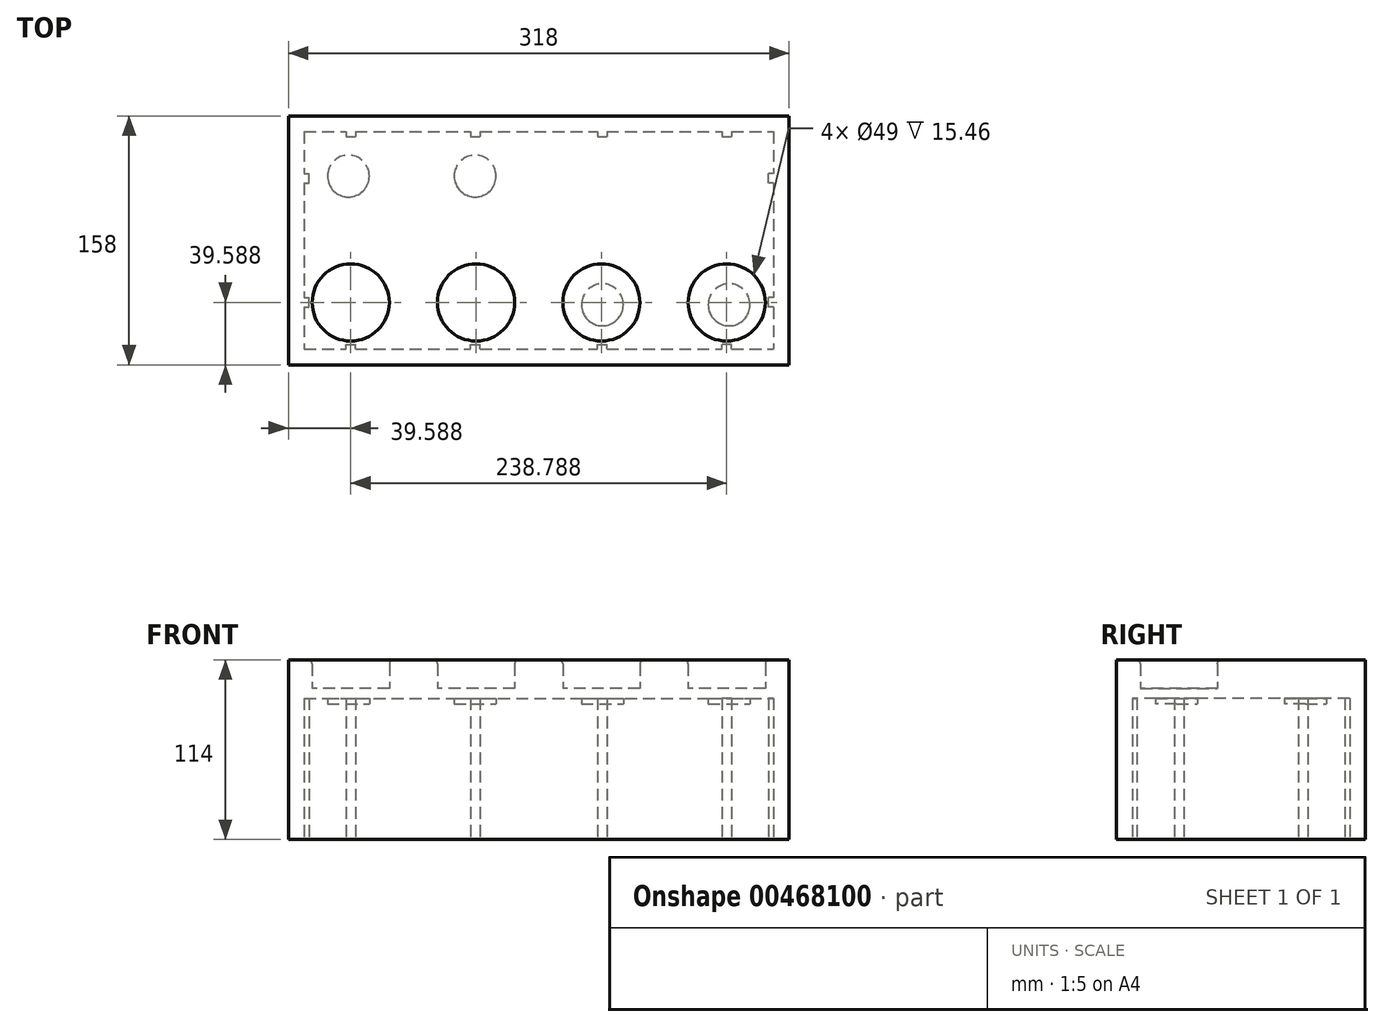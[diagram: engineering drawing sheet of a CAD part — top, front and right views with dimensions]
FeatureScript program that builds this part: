
annotation { "Feature Type Name" : "Feature", "Feature Type Description" : "" }
export const myFeature = defineFeature(function(context is Context, id is Id, definition is map)
    precondition{}
    {
        {
            var Q0;
            Q0=qCreatedBy(makeId("Top.planeOp"),FACE);
            var sketch = newSketch(context, id + "F0", { "sketchPlane" : qUnion([Q0])});
            skLineSegment(sketch, "E0.bottom", {"start": v(-159, 79) * mm, "end": v(159, 79) * mm});
            skLineSegment(sketch, "E0.top", {"start": v(-159, -79) * mm, "end": v(159, -79) * mm});
            skLineSegment(sketch, "E0.left", {"start": v(-159, 79) * mm, "end": v(-159, -79) * mm});
            skLineSegment(sketch, "E0.right", {"start": v(159, 79) * mm, "end": v(159, -79) * mm});
            skSolve(sketch);
        }
        {
            var Q0;
            Q0=makeQuery(id+"F0.imprint","IMPRINT",FACE,{"disambiguationData":[TD([[makeQuery(id+"F0.imprint","IMPRINT",EDGE,{"derivedFrom":sQuery(id+"F0.wireOp",EDGE,"E0.bottom")}),-1.0]])]});
            extrude(context, id + "F1", {"entities" : qUnion([Q0]), "depth" : 96 * mm});
        }
        {
            var Q0;
            Q0=makeQuery(id+"F1.opExtrude","CAP_FACE",FACE,{"disambiguationData":[OSD([sQuery(id+"F0.wireOp",EDGE,"E0.bottom"),sQuery(id+"F0.wireOp",EDGE,"E0.top"),sQuery(id+"F0.wireOp",EDGE,"E0.left"),sQuery(id+"F0.wireOp",EDGE,"E0.right")])],"isStart":true});
            shell(context, id + "F2", {"entities" : qUnion([Q0]), "thickness" : 10 * mm});
        }
        {
            var Q0;
            Q0=qCreatedBy(makeId("Top.planeOp"),FACE);
            var sketch = newSketch(context, id + "F3", { "sketchPlane" : qUnion([Q0])});
            skCircle(sketch, "E1", {"center": v(-80, 0) * mm, "radius": 32.05 * mm});
            skCircle(sketch, "E2", {"center": v(0, 0) * mm, "radius": 32.05 * mm});
            skCircle(sketch, "E3", {"center": v(80, 0) * mm, "radius": 32.05 * mm});
            skCircle(sketch, "E4", {"center": v(-80, 0) * mm, "radius": 24.5 * mm});
            skCircle(sketch, "E5", {"center": v(0, 0) * mm, "radius": 24.5 * mm});
            skCircle(sketch, "E6", {"center": v(80, 0) * mm, "radius": 24.5 * mm});
            skSolve(sketch);
        }
        {
            var Q0;
            Q0=makeQuery(id+"F3.imprint","IMPRINT",FACE,{"disambiguationData":[TD([[makeQuery(id+"F3.imprint","IMPRINT",EDGE,{"derivedFrom":sQuery(id+"F3.wireOp",EDGE,"E1")}),1.0]])]});
            var Q1;
            Q1=makeQuery(id+"F3.imprint","IMPRINT",FACE,{"disambiguationData":[TD([[makeQuery(id+"F3.imprint","IMPRINT",EDGE,{"derivedFrom":sQuery(id+"F3.wireOp",EDGE,"E2")}),1.0]])]});
            var Q2;
            Q2=makeQuery(id+"F3.imprint","IMPRINT",FACE,{"disambiguationData":[TD([[makeQuery(id+"F3.imprint","IMPRINT",EDGE,{"derivedFrom":sQuery(id+"F3.wireOp",EDGE,"E3")}),1.0]])]});
            extrude(context, id + "F4", {"entities" : qUnion([Q0, Q1, Q2]), "operationType" : NewBodyOperationType.ADD, "depth" : 94.74 * mm});
        }
        {
            var Q0;
            Q0=makeQuery(id+"F1.opExtrude","CAP_FACE",FACE,{"disambiguationData":[OSD([sQuery(id+"F0.wireOp",EDGE,"E0.bottom"),sQuery(id+"F0.wireOp",EDGE,"E0.top"),sQuery(id+"F0.wireOp",EDGE,"E0.left"),sQuery(id+"F0.wireOp",EDGE,"E0.right")])],"isStart":false});
            var sketch = newSketch(context, id + "F5", { "sketchPlane" : qUnion([Q0])});
            skCircle(sketch, "E7", {"center": v(-119.41, 39.41) * mm, "radius": 24.5 * mm});
            skCircle(sketch, "E8.1.0.0", {"center": v(-39.82, 39.41) * mm, "radius": 24.5 * mm});
            skCircle(sketch, "E8.2.0.0", {"center": v(39.78, 39.41) * mm, "radius": 24.5 * mm});
            skCircle(sketch, "E8.3.0.0", {"center": v(119.38, 39.41) * mm, "radius": 24.5 * mm});
            skLineSegment(sketch, "E8.direction1", {"start": v(-119.41, 39.41) * mm, "end": v(-39.82, 39.41) * mm, "construction": true});
            skLineSegment(sketch, "E9", {"start": v(-202.86, 0) * mm, "end": v(192.54, 0) * mm, "construction": true});
            skCircle(sketch, "E10.MirrorC", {"center": v(-119.41, -39.41) * mm, "radius": 24.5 * mm});
            skCircle(sketch, "E11.MirrorC", {"center": v(-39.82, -39.41) * mm, "radius": 24.5 * mm});
            skCircle(sketch, "E12.MirrorC", {"center": v(39.78, -39.41) * mm, "radius": 24.5 * mm});
            skCircle(sketch, "E13.MirrorC", {"center": v(119.38, -39.41) * mm, "radius": 24.5 * mm});
            skLineSegment(sketch, "E14", {"start": v(-186, 39.41) * mm, "end": v(210.43, 39.41) * mm, "construction": true});
            skLineSegment(sketch, "E15", {"start": v(-186.7, -39.41) * mm, "end": v(216.66, -39.41) * mm, "construction": true});
            skLineSegment(sketch, "E16", {"start": v(-119.41, 108.26) * mm, "end": v(-119.41, -106.32) * mm, "construction": true});
            skLineSegment(sketch, "E17", {"start": v(119.38, 102.92) * mm, "end": v(119.38, -102.76) * mm, "construction": true});
            skLineSegment(sketch, "E18", {"start": v(-39.82, 109.65) * mm, "end": v(-39.82, -100.32) * mm, "construction": true});
            skLineSegment(sketch, "E19", {"start": v(39.78, 106.53) * mm, "end": v(39.78, -109.25) * mm, "construction": true});
            skSolve(sketch);
        }
        {
            var Q0;
            Q0=makeQuery(id+"F5.imprint","IMPRINT",FACE,{"disambiguationData":[TD([[makeQuery(id+"F5.imprint","IMPRINT",EDGE,{"derivedFrom":sQuery(id+"F5.wireOp",EDGE,"E7")}),1.0]])]});
            var Q1;
            Q1=makeQuery(id+"F5.imprint","IMPRINT",FACE,{"disambiguationData":[TD([[makeQuery(id+"F5.imprint","IMPRINT",EDGE,{"derivedFrom":sQuery(id+"F5.wireOp",EDGE,"E8.1.0.0")}),1.0]])]});
            var Q2;
            Q2=makeQuery(id+"F5.imprint","IMPRINT",FACE,{"disambiguationData":[TD([[makeQuery(id+"F5.imprint","IMPRINT",EDGE,{"derivedFrom":sQuery(id+"F5.wireOp",EDGE,"E8.2.0.0")}),1.0]])]});
            var Q3;
            Q3=makeQuery(id+"F5.imprint","IMPRINT",FACE,{"disambiguationData":[TD([[makeQuery(id+"F5.imprint","IMPRINT",EDGE,{"derivedFrom":sQuery(id+"F5.wireOp",EDGE,"E8.3.0.0")}),1.0]])]});
            var Q4;
            Q4=makeQuery(id+"F5.imprint","IMPRINT",FACE,{"disambiguationData":[TD([[makeQuery(id+"F5.imprint","IMPRINT",EDGE,{"derivedFrom":sQuery(id+"F5.wireOp",EDGE,"E13.MirrorC")}),-1.0]])]});
            var Q5;
            Q5=makeQuery(id+"F5.imprint","IMPRINT",FACE,{"disambiguationData":[TD([[makeQuery(id+"F5.imprint","IMPRINT",EDGE,{"derivedFrom":sQuery(id+"F5.wireOp",EDGE,"E12.MirrorC")}),-1.0]])]});
            var Q6;
            Q6=makeQuery(id+"F5.imprint","IMPRINT",FACE,{"disambiguationData":[TD([[makeQuery(id+"F5.imprint","IMPRINT",EDGE,{"derivedFrom":sQuery(id+"F5.wireOp",EDGE,"E11.MirrorC")}),-1.0]])]});
            var Q7;
            Q7=makeQuery(id+"F5.imprint","IMPRINT",FACE,{"disambiguationData":[TD([[makeQuery(id+"F5.imprint","IMPRINT",EDGE,{"derivedFrom":sQuery(id+"F5.wireOp",EDGE,"E10.MirrorC")}),-1.0]])]});
            extrude(context, id + "F6", {"entities" : qUnion([Q0, Q1, Q2, Q3, Q4, Q5, Q6, Q7]), "operationType" : NewBodyOperationType.ADD, "depth" : 18 * mm});
        }
        {
            var Q0;
            Q0=makeQuery(id+"F4.boolean.opBoolean","MERGE",FACE,{"derivedFrom":[makeQuery(id+"F1.opExtrude","CAP_FACE",FACE,{"disambiguationData":[OSD([sQuery(id+"F0.wireOp",EDGE,"E0.bottom"),sQuery(id+"F0.wireOp",EDGE,"E0.top"),sQuery(id+"F0.wireOp",EDGE,"E0.left"),sQuery(id+"F0.wireOp",EDGE,"E0.right")])],"isStart":true}),makeQuery(id+"F4.opExtrude","CAP_FACE",FACE,{"disambiguationData":[OSD([sQuery(id+"F9.wireOp",EDGE,"E38.bottom"),sQuery(id+"F9.wireOp",EDGE,"E38.top"),sQuery(id+"F9.wireOp",EDGE,"E38.left"),sQuery(id+"F9.wireOp",EDGE,"E38.right")])],"isStart":true}),makeQuery(id+"F4.opExtrude","CAP_FACE",FACE,{"disambiguationData":[OSD([sQuery(id+"F3.wireOp",EDGE,"E2"),sQuery(id+"F3.wireOp",EDGE,"E5")])],"isStart":true})]});
            var sketch = newSketch(context, id + "F7", { "sketchPlane" : qUnion([Q0])});
            skLineSegment(sketch, "E20.bottom", {"start": v(-122.42, 73.6) * mm, "end": v(-116.42, 73.6) * mm});
            skLineSegment(sketch, "E20.top", {"start": v(-122.42, 66) * mm, "end": v(-116.42, 66) * mm});
            skLineSegment(sketch, "E20.left", {"start": v(-122.42, 73.6) * mm, "end": v(-122.42, 66) * mm});
            skLineSegment(sketch, "E20.right", {"start": v(-116.42, 73.6) * mm, "end": v(-116.42, 66) * mm});
            skLineSegment(sketch, "E21.bottom", {"start": v(-154.66, 42.42) * mm, "end": v(-146, 42.42) * mm});
            skLineSegment(sketch, "E21.top", {"start": v(-154.66, 36.42) * mm, "end": v(-146, 36.42) * mm});
            skLineSegment(sketch, "E21.left", {"start": v(-154.66, 42.42) * mm, "end": v(-154.66, 36.42) * mm});
            skLineSegment(sketch, "E21.right", {"start": v(-146, 42.42) * mm, "end": v(-146, 36.42) * mm});
            skLineSegment(sketch, "E22.bottom", {"start": v(-154.5, -36.42) * mm, "end": v(-146, -36.42) * mm});
            skLineSegment(sketch, "E22.top", {"start": v(-154.5, -42.42) * mm, "end": v(-146, -42.42) * mm});
            skLineSegment(sketch, "E22.left", {"start": v(-154.5, -36.42) * mm, "end": v(-154.5, -42.42) * mm});
            skLineSegment(sketch, "E22.right", {"start": v(-146, -36.42) * mm, "end": v(-146, -42.42) * mm});
            skLineSegment(sketch, "E23.bottom", {"start": v(-122.42, -72.53) * mm, "end": v(-116.42, -72.53) * mm});
            skLineSegment(sketch, "E23.top", {"start": v(-122.42, -66) * mm, "end": v(-116.42, -66) * mm});
            skLineSegment(sketch, "E23.left", {"start": v(-122.42, -72.53) * mm, "end": v(-122.42, -66) * mm});
            skLineSegment(sketch, "E23.right", {"start": v(-116.42, -72.53) * mm, "end": v(-116.42, -66) * mm});
            skLineSegment(sketch, "E24.bottom", {"start": v(122.42, 74.33) * mm, "end": v(116.42, 74.33) * mm});
            skLineSegment(sketch, "E24.top", {"start": v(122.42, 66) * mm, "end": v(116.42, 66) * mm});
            skLineSegment(sketch, "E24.left", {"start": v(122.42, 74.33) * mm, "end": v(122.42, 66) * mm});
            skLineSegment(sketch, "E24.right", {"start": v(116.42, 74.33) * mm, "end": v(116.42, 66) * mm});
            skLineSegment(sketch, "E25.bottom", {"start": v(152.85, 42.42) * mm, "end": v(146, 42.42) * mm});
            skLineSegment(sketch, "E25.top", {"start": v(152.85, 36.42) * mm, "end": v(146, 36.42) * mm});
            skLineSegment(sketch, "E25.left", {"start": v(152.85, 42.42) * mm, "end": v(152.85, 36.42) * mm});
            skLineSegment(sketch, "E25.right", {"start": v(146, 42.42) * mm, "end": v(146, 36.42) * mm});
            skLineSegment(sketch, "E26.bottom", {"start": v(116.42, -72.71) * mm, "end": v(122.42, -72.71) * mm});
            skLineSegment(sketch, "E26.top", {"start": v(116.42, -66) * mm, "end": v(122.42, -66) * mm});
            skLineSegment(sketch, "E26.left", {"start": v(116.42, -72.71) * mm, "end": v(116.42, -66) * mm});
            skLineSegment(sketch, "E26.right", {"start": v(122.42, -72.71) * mm, "end": v(122.42, -66) * mm});
            skLineSegment(sketch, "E27.bottom", {"start": v(153.22, -36.42) * mm, "end": v(146, -36.42) * mm});
            skLineSegment(sketch, "E27.top", {"start": v(153.22, -42.42) * mm, "end": v(146, -42.42) * mm});
            skLineSegment(sketch, "E27.left", {"start": v(153.22, -36.42) * mm, "end": v(153.22, -42.42) * mm});
            skLineSegment(sketch, "E27.right", {"start": v(146, -36.42) * mm, "end": v(146, -42.42) * mm});
            skLineSegment(sketch, "E28.bottom", {"start": v(-43.28, 73.4) * mm, "end": v(-37.28, 73.4) * mm});
            skLineSegment(sketch, "E28.top", {"start": v(-43.28, 66) * mm, "end": v(-37.28, 66) * mm});
            skLineSegment(sketch, "E28.left", {"start": v(-43.28, 73.4) * mm, "end": v(-43.28, 66) * mm});
            skLineSegment(sketch, "E28.right", {"start": v(-37.28, 73.4) * mm, "end": v(-37.28, 66) * mm});
            skLineSegment(sketch, "E29.MirrorCS", {"start": v(-43.28, -66) * mm, "end": v(-37.28, -66) * mm});
            skLineSegment(sketch, "E30.MirrorCS", {"start": v(-43.28, -73.4) * mm, "end": v(-43.28, -66) * mm});
            skLineSegment(sketch, "E31.MirrorCS", {"start": v(-37.28, -73.4) * mm, "end": v(-37.28, -66) * mm});
            skLineSegment(sketch, "E32.MirrorCS", {"start": v(-43.28, -73.4) * mm, "end": v(-37.28, -73.4) * mm});
            skLineSegment(sketch, "E33.bottom", {"start": v(37.28, 73.15) * mm, "end": v(43.28, 73.15) * mm});
            skLineSegment(sketch, "E33.top", {"start": v(37.28, 66) * mm, "end": v(43.28, 66) * mm});
            skLineSegment(sketch, "E33.left", {"start": v(37.28, 73.15) * mm, "end": v(37.28, 66) * mm});
            skLineSegment(sketch, "E33.right", {"start": v(43.28, 73.15) * mm, "end": v(43.28, 66) * mm});
            skLineSegment(sketch, "E34.MirrorCS", {"start": v(43.28, -73.15) * mm, "end": v(43.28, -66) * mm});
            skLineSegment(sketch, "E35.MirrorCS", {"start": v(37.28, -73.15) * mm, "end": v(37.28, -66) * mm});
            skLineSegment(sketch, "E36.MirrorCS", {"start": v(37.28, -66) * mm, "end": v(43.28, -66) * mm});
            skLineSegment(sketch, "E37.MirrorCS", {"start": v(37.28, -73.15) * mm, "end": v(43.28, -73.15) * mm});
            skSolve(sketch);
        }
        {
            var Q0;
            {var subQ0=sQuery(id+"F7.wireOp",EDGE,"E33.top");Q0=makeQuery(id+"F7.imprint","IMPRINT",FACE,{"disambiguationData":[TD([[makeQuery(id+"F7.imprint","IMPRINT",EDGE,{"derivedFrom":subQ0}),1.0]])]});}
            var Q1;
            {var subQ0=sQuery(id+"F7.wireOp",EDGE,"E24.top");Q1=makeQuery(id+"F7.imprint","IMPRINT",FACE,{"disambiguationData":[TD([[makeQuery(id+"F7.imprint","IMPRINT",EDGE,{"derivedFrom":subQ0}),-1.0]])]});}
            var Q2;
            {var subQ0=sQuery(id+"F7.wireOp",EDGE,"E25.right");Q2=makeQuery(id+"F7.imprint","IMPRINT",FACE,{"disambiguationData":[TD([[makeQuery(id+"F7.imprint","IMPRINT",EDGE,{"derivedFrom":subQ0}),1.0]])]});}
            var Q3;
            {var subQ0=sQuery(id+"F7.wireOp",EDGE,"E28.top");Q3=makeQuery(id+"F7.imprint","IMPRINT",FACE,{"disambiguationData":[TD([[makeQuery(id+"F7.imprint","IMPRINT",EDGE,{"derivedFrom":subQ0}),1.0]])]});}
            var Q4;
            {var subQ0=sQuery(id+"F7.wireOp",EDGE,"E20.top");Q4=makeQuery(id+"F7.imprint","IMPRINT",FACE,{"disambiguationData":[TD([[makeQuery(id+"F7.imprint","IMPRINT",EDGE,{"derivedFrom":subQ0}),1.0]])]});}
            var Q5;
            {var subQ0=sQuery(id+"F7.wireOp",EDGE,"E21.right");Q5=makeQuery(id+"F7.imprint","IMPRINT",FACE,{"disambiguationData":[TD([[makeQuery(id+"F7.imprint","IMPRINT",EDGE,{"derivedFrom":subQ0}),-1.0]])]});}
            var Q6;
            {var subQ0=sQuery(id+"F7.wireOp",EDGE,"E22.right");Q6=makeQuery(id+"F7.imprint","IMPRINT",FACE,{"disambiguationData":[TD([[makeQuery(id+"F7.imprint","IMPRINT",EDGE,{"derivedFrom":subQ0}),-1.0]])]});}
            var Q7;
            {var subQ0=sQuery(id+"F7.wireOp",EDGE,"E23.top");Q7=makeQuery(id+"F7.imprint","IMPRINT",FACE,{"disambiguationData":[TD([[makeQuery(id+"F7.imprint","IMPRINT",EDGE,{"derivedFrom":subQ0}),-1.0]])]});}
            var Q8;
            {var subQ0=sQuery(id+"F7.wireOp",EDGE,"E29.MirrorCS");Q8=makeQuery(id+"F7.imprint","IMPRINT",FACE,{"disambiguationData":[TD([[makeQuery(id+"F7.imprint","IMPRINT",EDGE,{"derivedFrom":subQ0}),-1.0]])]});}
            var Q9;
            {var subQ0=sQuery(id+"F7.wireOp",EDGE,"E36.MirrorCS");Q9=makeQuery(id+"F7.imprint","IMPRINT",FACE,{"disambiguationData":[TD([[makeQuery(id+"F7.imprint","IMPRINT",EDGE,{"derivedFrom":subQ0}),-1.0]])]});}
            var Q10;
            {var subQ0=sQuery(id+"F7.wireOp",EDGE,"E26.top");Q10=makeQuery(id+"F7.imprint","IMPRINT",FACE,{"disambiguationData":[TD([[makeQuery(id+"F7.imprint","IMPRINT",EDGE,{"derivedFrom":subQ0}),-1.0]])]});}
            var Q11;
            {var subQ0=sQuery(id+"F7.wireOp",EDGE,"E27.right");Q11=makeQuery(id+"F7.imprint","IMPRINT",FACE,{"disambiguationData":[TD([[makeQuery(id+"F7.imprint","IMPRINT",EDGE,{"derivedFrom":subQ0}),1.0]])]});}
            extrude(context, id + "F8", {"entities" : qUnion([Q0, Q1, Q2, Q3, Q4, Q5, Q6, Q7, Q8, Q9, Q10, Q11]), "operationType" : NewBodyOperationType.ADD, "oppositeDirection" : true, "depth" : 96 * mm});
        }
        {
            var Q0;
            Q0=qCreatedBy(makeId("Top.planeOp"),FACE);
            var sketch = newSketch(context, id + "F9", { "sketchPlane" : qUnion([Q0])});
            skLineSegment(sketch, "E38.bottom", {"start": v(-4.45, -79) * mm, "end": v(3.55, -79) * mm});
            skLineSegment(sketch, "E38.top", {"start": v(-4.45, 79) * mm, "end": v(3.55, 79) * mm});
            skLineSegment(sketch, "E38.left", {"start": v(-4.45, -79) * mm, "end": v(-4.45, -31.74) * mm});
            skLineSegment(sketch, "E38.right", {"start": v(3.55, -79) * mm, "end": v(3.55, -31.85) * mm});
            skArc(sketch, "E39.0", {"start": v(-4.45, -31.74) * mm, "mid": v(-0.45, -32.05) * mm, "end": v(3.55, -31.85) * mm});
            skLineSegment(sketch, "E40.trimOffspring", {"start": v(3.55, 31.85) * mm, "end": v(3.55, 79) * mm});
            skLineSegment(sketch, "E41.trimOffspring", {"start": v(-4.45, 31.74) * mm, "end": v(-4.45, 79) * mm});
            skArc(sketch, "E42.trimOffspring", {"start": v(3.55, 31.85) * mm, "mid": v(-0.45, 32.05) * mm, "end": v(-4.45, 31.74) * mm});
            skSolve(sketch);
        }
        {
            var Q0;
            Q0=qSketchRegion(id+"F9",true);
            var Q1;
            {var subQ0=sQuery(id+"F0.wireOp",EDGE,"E0.right");var subQ1=sQuery(id+"F0.wireOp",EDGE,"E0.left");var subQ2=sQuery(id+"F0.wireOp",EDGE,"E0.top");var subQ3=sQuery(id+"F0.wireOp",EDGE,"E0.bottom");Q1=makeQuery(id+"F4.boolean.opBoolean","SPLIT",FACE,{"disambiguationData":[TD([makeQuery(id+"F2.opShell","OFFSET_FACE",FACE,{"disambiguationData":[OSD([subQ3])]})])],"derivedFrom":makeQuery(id+"F2.opShell","OFFSET_FACE",FACE,{"disambiguationData":[OSD([subQ3,subQ2,subQ1,subQ0])]})});}
            extrude(context, id + "F10", {"entities" : qUnion([Q0]), "operationType" : NewBodyOperationType.ADD, "endBound" : BoundingType.UP_TO_SURFACE, "endBoundEntityFace" : qUnion([Q1]), "depth" : 25.4 * mm, "hasSecondDirection" : true, "secondDirectionOppositeDirection" : false, "secondDirectionDepth" : 6.6 * mm});
        }
        {
            var Q0;
            Q0=makeQuery(id+"F6.opExtrude","CAP_EDGE",EDGE,{"disambiguationData":[OSD([sQuery(id+"F5.wireOp",EDGE,"E10.MirrorC")])],"isStart":false});
            var Q1;
            Q1=makeQuery(id+"F6.opExtrude","CAP_EDGE",EDGE,{"disambiguationData":[OSD([sQuery(id+"F5.wireOp",EDGE,"E7")])],"isStart":false});
            var Q2;
            Q2=makeQuery(id+"F6.opExtrude","CAP_EDGE",EDGE,{"disambiguationData":[OSD([sQuery(id+"F5.wireOp",EDGE,"E8.1.0.0")])],"isStart":false});
            var Q3;
            Q3=makeQuery(id+"F6.opExtrude","CAP_EDGE",EDGE,{"disambiguationData":[OSD([sQuery(id+"F5.wireOp",EDGE,"E11.MirrorC")])],"isStart":false});
            var Q4;
            Q4=makeQuery(id+"F6.opExtrude","CAP_EDGE",EDGE,{"disambiguationData":[OSD([sQuery(id+"F5.wireOp",EDGE,"E12.MirrorC")])],"isStart":false});
            var Q5;
            Q5=makeQuery(id+"F6.opExtrude","CAP_EDGE",EDGE,{"disambiguationData":[OSD([sQuery(id+"F5.wireOp",EDGE,"E8.2.0.0")])],"isStart":false});
            var Q6;
            Q6=makeQuery(id+"F6.opExtrude","CAP_EDGE",EDGE,{"disambiguationData":[OSD([sQuery(id+"F5.wireOp",EDGE,"E8.3.0.0")])],"isStart":false});
            var Q7;
            Q7=makeQuery(id+"F6.opExtrude","CAP_EDGE",EDGE,{"disambiguationData":[OSD([sQuery(id+"F5.wireOp",EDGE,"E13.MirrorC")])],"isStart":false});
            var Q8;
            Q8=makeQuery(id+"F6.opExtrude","CAP_EDGE",EDGE,{"disambiguationData":[OSD([sQuery(id+"F5.wireOp",EDGE,"E13.MirrorC")])],"isStart":true});
            var Q9;
            Q9=makeQuery(id+"F6.opExtrude","CAP_EDGE",EDGE,{"disambiguationData":[OSD([sQuery(id+"F5.wireOp",EDGE,"E8.3.0.0")])],"isStart":true});
            var Q10;
            Q10=makeQuery(id+"F6.opExtrude","CAP_EDGE",EDGE,{"disambiguationData":[OSD([sQuery(id+"F5.wireOp",EDGE,"E12.MirrorC")])],"isStart":true});
            var Q11;
            Q11=makeQuery(id+"F6.opExtrude","CAP_EDGE",EDGE,{"disambiguationData":[OSD([sQuery(id+"F5.wireOp",EDGE,"E11.MirrorC")])],"isStart":true});
            var Q12;
            Q12=makeQuery(id+"F6.opExtrude","CAP_EDGE",EDGE,{"disambiguationData":[OSD([sQuery(id+"F5.wireOp",EDGE,"E10.MirrorC")])],"isStart":true});
            var Q13;
            Q13=makeQuery(id+"F6.opExtrude","CAP_EDGE",EDGE,{"disambiguationData":[OSD([sQuery(id+"F5.wireOp",EDGE,"E7")])],"isStart":true});
            var Q14;
            Q14=makeQuery(id+"F6.opExtrude","CAP_EDGE",EDGE,{"disambiguationData":[OSD([sQuery(id+"F5.wireOp",EDGE,"E8.1.0.0")])],"isStart":true});
            var Q15;
            Q15=makeQuery(id+"F6.opExtrude","CAP_EDGE",EDGE,{"disambiguationData":[OSD([sQuery(id+"F5.wireOp",EDGE,"E8.2.0.0")])],"isStart":true});
            fillet(context, id + "F11", {"entities" : qUnion([Q0, Q1, Q2, Q3, Q4, Q5, Q6, Q7, Q8, Q9, Q10, Q11, Q12, Q13, Q14, Q15]), "radius" : 2.54 * mm, "tangentPropagation" : true, "allowEdgeOverflow" : false});
        }
        {
            var Q0;
            {var subQ0=sQuery(id+"F0.wireOp",EDGE,"E0.bottom");var subQ1=sQuery(id+"F0.wireOp",EDGE,"E0.top");var subQ2=sQuery(id+"F0.wireOp",EDGE,"E0.right");var subQ3=sQuery(id+"F0.wireOp",EDGE,"E0.left");Q0=makeQuery(id+"F8.boolean.opBoolean","MERGE",FACE,{"derivedFrom":[makeQuery(id+"F1.opExtrude","CAP_FACE",FACE,{"disambiguationData":[OSD([subQ0,subQ1,subQ3,subQ2])],"isStart":true}),makeQuery(id+"F8.opExtrude","CAP_FACE",FACE,{"disambiguationData":[OSD([subQ1,sQuery(id+"F7.wireOp",EDGE,"E20.top"),sQuery(id+"F7.wireOp",EDGE,"E20.left"),sQuery(id+"F7.wireOp",EDGE,"E20.right")])],"isStart":true}),makeQuery(id+"F8.opExtrude","CAP_FACE",FACE,{"disambiguationData":[OSD([subQ3,sQuery(id+"F7.wireOp",EDGE,"E21.bottom"),sQuery(id+"F7.wireOp",EDGE,"E21.top"),sQuery(id+"F7.wireOp",EDGE,"E21.right")])],"isStart":true}),makeQuery(id+"F8.opExtrude","CAP_FACE",FACE,{"disambiguationData":[OSD([subQ3,sQuery(id+"F7.wireOp",EDGE,"E22.bottom"),sQuery(id+"F7.wireOp",EDGE,"E22.top"),sQuery(id+"F7.wireOp",EDGE,"E22.right")])],"isStart":true}),makeQuery(id+"F8.opExtrude","CAP_FACE",FACE,{"disambiguationData":[OSD([subQ0,sQuery(id+"F7.wireOp",EDGE,"E23.top"),sQuery(id+"F7.wireOp",EDGE,"E23.left"),sQuery(id+"F7.wireOp",EDGE,"E23.right")])],"isStart":true}),makeQuery(id+"F8.opExtrude","CAP_FACE",FACE,{"disambiguationData":[OSD([subQ1,sQuery(id+"F7.wireOp",EDGE,"E24.top"),sQuery(id+"F7.wireOp",EDGE,"E24.left"),sQuery(id+"F7.wireOp",EDGE,"E24.right")])],"isStart":true}),makeQuery(id+"F8.opExtrude","CAP_FACE",FACE,{"disambiguationData":[OSD([subQ2,sQuery(id+"F7.wireOp",EDGE,"E25.bottom"),sQuery(id+"F7.wireOp",EDGE,"E25.top"),sQuery(id+"F7.wireOp",EDGE,"E25.right")])],"isStart":true}),makeQuery(id+"F8.opExtrude","CAP_FACE",FACE,{"disambiguationData":[OSD([subQ0,sQuery(id+"F7.wireOp",EDGE,"E26.top"),sQuery(id+"F7.wireOp",EDGE,"E26.left"),sQuery(id+"F7.wireOp",EDGE,"E26.right")])],"isStart":true}),makeQuery(id+"F8.opExtrude","CAP_FACE",FACE,{"disambiguationData":[OSD([subQ2,sQuery(id+"F7.wireOp",EDGE,"E27.bottom"),sQuery(id+"F7.wireOp",EDGE,"E27.top"),sQuery(id+"F7.wireOp",EDGE,"E27.right")])],"isStart":true}),makeQuery(id+"F8.opExtrude","CAP_FACE",FACE,{"disambiguationData":[OSD([subQ1,sQuery(id+"F7.wireOp",EDGE,"E28.top"),sQuery(id+"F7.wireOp",EDGE,"E28.left"),sQuery(id+"F7.wireOp",EDGE,"E28.right")])],"isStart":true}),makeQuery(id+"F8.opExtrude","CAP_FACE",FACE,{"disambiguationData":[OSD([subQ0,sQuery(id+"F7.wireOp",EDGE,"E29.MirrorCS"),sQuery(id+"F7.wireOp",EDGE,"E30.MirrorCS"),sQuery(id+"F7.wireOp",EDGE,"E31.MirrorCS")])],"isStart":true}),makeQuery(id+"F8.opExtrude","CAP_FACE",FACE,{"disambiguationData":[OSD([subQ1,sQuery(id+"F7.wireOp",EDGE,"E33.top"),sQuery(id+"F7.wireOp",EDGE,"E33.left"),sQuery(id+"F7.wireOp",EDGE,"E33.right")])],"isStart":true}),makeQuery(id+"F8.opExtrude","CAP_FACE",FACE,{"disambiguationData":[OSD([subQ0,sQuery(id+"F7.wireOp",EDGE,"E34.MirrorCS"),sQuery(id+"F7.wireOp",EDGE,"E35.MirrorCS"),sQuery(id+"F7.wireOp",EDGE,"E36.MirrorCS")])],"isStart":true})]});}
            var sketch = newSketch(context, id + "F12", { "sketchPlane" : qUnion([Q0])});
            skCircle(sketch, "E43", {"center": v(-120.9, 40.9) * mm, "radius": 13.3 * mm});
            skLineSegment(sketch, "E44", {"start": v(-120.9, 40.9) * mm, "end": v(-120.9, 79) * mm, "construction": true});
            skLineSegment(sketch, "E45", {"start": v(-120.9, 40.9) * mm, "end": v(-159, 40.9) * mm, "construction": true});
            skLineSegment(sketch, "E46", {"start": v(-159, 0) * mm, "end": v(159, 0) * mm, "construction": true});
            skCircle(sketch, "E47.MirrorC", {"center": v(-120.9, -40.9) * mm, "radius": 13.3 * mm});
            skLineSegment(sketch, "E48", {"start": v(0, 79) * mm, "end": v(0, -79) * mm, "construction": true});
            skCircle(sketch, "E49.MirrorC", {"center": v(120.9, -40.9) * mm, "radius": 13.3 * mm});
            skCircle(sketch, "E50.MirrorC", {"center": v(120.9, 40.9) * mm, "radius": 13.3 * mm});
            skLineSegment(sketch, "E51", {"start": v(-80.77, 32.16) * mm, "end": v(0, 32.16) * mm, "construction": true});
            skLineSegment(sketch, "E52", {"start": v(-40.39, 32.16) * mm, "end": v(-40.51, 79.36) * mm, "construction": true});
            skCircle(sketch, "E53", {"center": v(-40.4, 40.9) * mm, "radius": 13.3 * mm});
            skLineSegment(sketch, "E54", {"start": v(-120.9, 40.9) * mm, "end": v(120.9, 40.9) * mm, "construction": true});
            skCircle(sketch, "E55.MirrorC", {"center": v(40.4, 40.9) * mm, "radius": 13.3 * mm});
            skCircle(sketch, "E56.MirrorC", {"center": v(40.4, -40.9) * mm, "radius": 13.3 * mm});
            skCircle(sketch, "E57.MirrorC", {"center": v(-40.4, -40.9) * mm, "radius": 13.3 * mm});
            skSolve(sketch);
        }
        {
            var Q0;
            Q0=makeQuery(id+"F12.imprint","IMPRINT",FACE,{"disambiguationData":[TD([[makeQuery(id+"F12.imprint","IMPRINT",EDGE,{"derivedFrom":sQuery(id+"F12.wireOp",EDGE,"E49.MirrorC")}),1.0]])]});
            var Q1;
            Q1=makeQuery(id+"F12.imprint","IMPRINT",FACE,{"disambiguationData":[TD([[makeQuery(id+"F12.imprint","IMPRINT",EDGE,{"derivedFrom":sQuery(id+"F12.wireOp",EDGE,"E56.MirrorC")}),1.0]])]});
            var Q2;
            Q2=makeQuery(id+"F12.imprint","IMPRINT",FACE,{"disambiguationData":[TD([[makeQuery(id+"F12.imprint","IMPRINT",EDGE,{"derivedFrom":sQuery(id+"F12.wireOp",EDGE,"E57.MirrorC")}),-1.0]])]});
            var Q3;
            Q3=makeQuery(id+"F12.imprint","IMPRINT",FACE,{"disambiguationData":[TD([[makeQuery(id+"F12.imprint","IMPRINT",EDGE,{"derivedFrom":sQuery(id+"F12.wireOp",EDGE,"E47.MirrorC")}),-1.0]])]});
            var Q4;
            Q4=makeQuery(id+"F12.imprint","IMPRINT",FACE,{"disambiguationData":[TD([[makeQuery(id+"F12.imprint","IMPRINT",EDGE,{"derivedFrom":sQuery(id+"F12.wireOp",EDGE,"E43")}),1.0]])]});
            var Q5;
            Q5=makeQuery(id+"F12.imprint","IMPRINT",FACE,{"disambiguationData":[TD([[makeQuery(id+"F12.imprint","IMPRINT",EDGE,{"derivedFrom":sQuery(id+"F12.wireOp",EDGE,"E53")}),1.0]])]});
            var Q6;
            Q6=makeQuery(id+"F12.imprint","IMPRINT",FACE,{"disambiguationData":[TD([[makeQuery(id+"F12.imprint","IMPRINT",EDGE,{"derivedFrom":sQuery(id+"F12.wireOp",EDGE,"E55.MirrorC")}),-1.0]])]});
            var Q7;
            Q7=makeQuery(id+"F12.imprint","IMPRINT",FACE,{"disambiguationData":[TD([[makeQuery(id+"F12.imprint","IMPRINT",EDGE,{"derivedFrom":sQuery(id+"F12.wireOp",EDGE,"E50.MirrorC")}),-1.0]])]});
            var Q8;
            Q8=sQuery(id+"F12.wireOp",EDGE,"E43");
            extrude(context, id + "F13", {"entities" : qUnion([Q0, Q1, Q2, Q3, Q4, Q5, Q6, Q7]), "operationType" : NewBodyOperationType.REMOVE, "surfaceEntities" : qUnion([Q8]), "oppositeDirection" : true, "depth" : 89.66 * mm});
        }
    });
